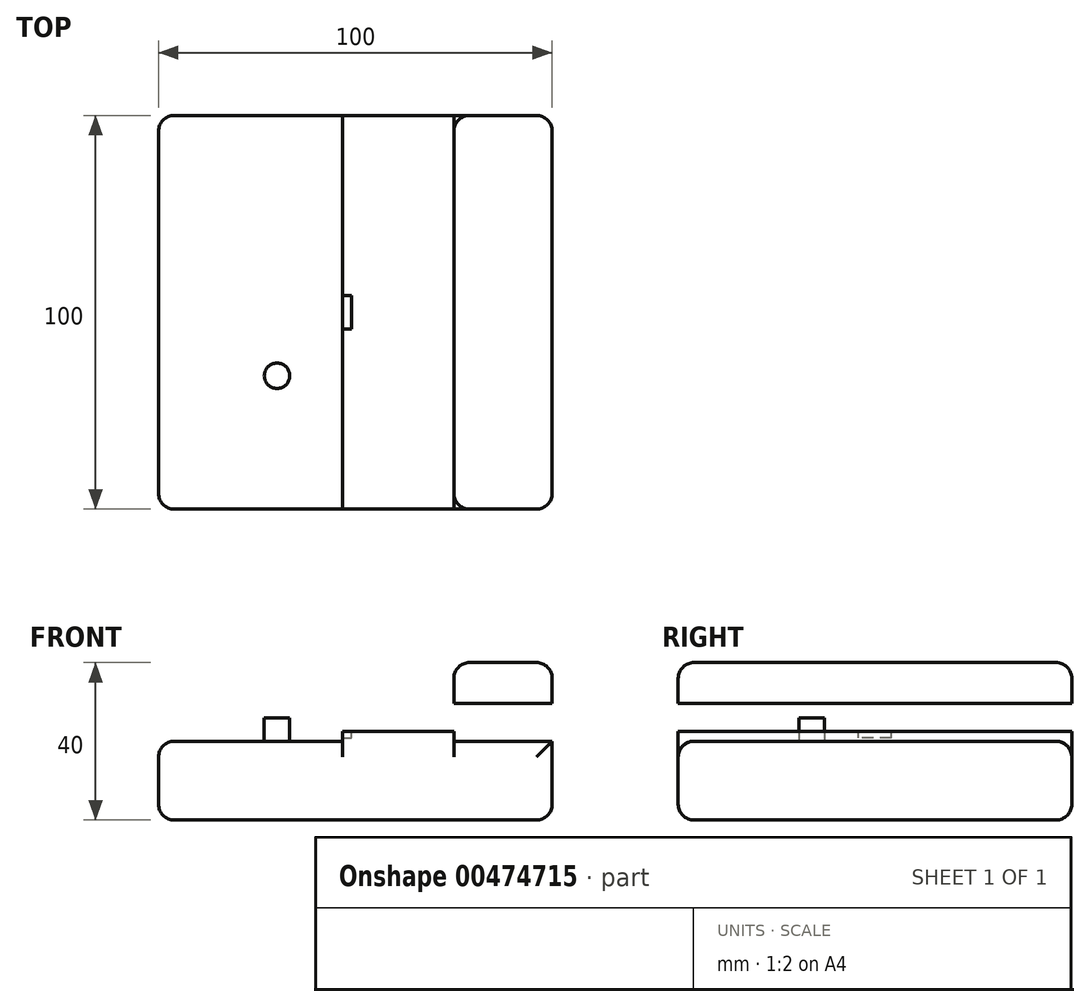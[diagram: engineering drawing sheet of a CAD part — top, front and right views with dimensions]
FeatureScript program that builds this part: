
annotation { "Feature Type Name" : "Feature", "Feature Type Description" : "" }
export const myFeature = defineFeature(function(context is Context, id is Id, definition is map)
    precondition{}
    {
        {
            var Q0;
            Q0=qCreatedBy(makeId("Top.planeOp"),FACE);
            var sketch = newSketch(context, id + "F0", { "sketchPlane" : qUnion([Q0])});
            skLineSegment(sketch, "E0.bottom", {"start": v(50, -50) * mm, "end": v(-50, -50) * mm});
            skLineSegment(sketch, "E0.top", {"start": v(50, 50) * mm, "end": v(-50, 50) * mm});
            skLineSegment(sketch, "E0.left", {"start": v(50, -50) * mm, "end": v(50, 50) * mm});
            skLineSegment(sketch, "E0.right", {"start": v(-50, -50) * mm, "end": v(-50, 50) * mm});
            skPoint(sketch, "E0.middle", {"position": v(0, 0) * mm});
            skSolve(sketch);
        }
        {
            var Q0;
            Q0=makeQuery(id+"F0.imprint","IMPRINT",FACE,{"disambiguationData":[TD([[makeQuery(id+"F0.imprint","IMPRINT",EDGE,{"derivedFrom":sQuery(id+"F0.wireOp",EDGE,"E0.bottom")}),-1.0]])]});
            extrude(context, id + "F1", {"entities" : qUnion([Q0]), "endBound" : BoundingType.SYMMETRIC, "depth" : 20 * mm, "offsetDistance" : 25 * mm});
        }
        {
            var Q0;
            Q0=makeQuery(id+"F1.opExtrude","CAP_FACE",FACE,{"disambiguationData":[OSD([sQuery(id+"F0.wireOp",EDGE,"E0.bottom"),sQuery(id+"F0.wireOp",EDGE,"E0.top"),sQuery(id+"F0.wireOp",EDGE,"E0.left"),sQuery(id+"F0.wireOp",EDGE,"E0.right")])],"isStart":false});
            var sketch = newSketch(context, id + "F2", { "sketchPlane" : qUnion([Q0])});
            skLineSegment(sketch, "E1.0.0", {"start": v(50, -50) * mm, "end": v(50, 50) * mm});
            skLineSegment(sketch, "E1.0.1", {"start": v(50, 50) * mm, "end": v(-50, 50) * mm});
            skLineSegment(sketch, "E1.0.2", {"start": v(-50, 50) * mm, "end": v(-50, -50) * mm});
            skLineSegment(sketch, "E1.0.3", {"start": v(-50, -50) * mm, "end": v(50, -50) * mm});
            skLineSegment(sketch, "E2", {"start": v(25, 0) * mm, "end": v(25, -50) * mm});
            skLineSegment(sketch, "E3", {"start": v(25, -50) * mm, "end": v(25, 50) * mm});
            skPoint(sketch, "E4.start.orphan", {"position": v(50, 0) * mm});
            skSolve(sketch);
        }
        {
            var Q0;
            Q0=makeQuery(id+"F1.opExtrude","SWEPT_FACE",FACE,{"disambiguationData":[OSD([sQuery(id+"F0.wireOp",EDGE,"E0.bottom")])]});
            var sketch = newSketch(context, id + "F3", { "sketchPlane" : qUnion([Q0])});
            skLineSegment(sketch, "E5.0.0", {"start": v(-50, -10) * mm, "end": v(50, -10) * mm});
            skLineSegment(sketch, "E5.0.1", {"start": v(50, -10) * mm, "end": v(50, 10) * mm});
            skLineSegment(sketch, "E5.0.2", {"start": v(50, 10) * mm, "end": v(-50, 10) * mm});
            skLineSegment(sketch, "E5.0.3", {"start": v(-50, 10) * mm, "end": v(-50, -10) * mm});
            skLineSegment(sketch, "E6", {"start": v(50, 10) * mm, "end": v(25, 10) * mm});
            skLineSegment(sketch, "E7", {"start": v(25, 10) * mm, "end": v(0, 10) * mm});
            skLineSegment(sketch, "E8", {"start": v(0, 10) * mm, "end": v(0, 22.2) * mm});
            skLineSegment(sketch, "E9", {"start": v(0, 16.1) * mm, "end": v(25, 16.1) * mm});
            skLineSegment(sketch, "E10", {"start": v(25, 16.1) * mm, "end": v(25, 12.56) * mm});
            skLineSegment(sketch, "E11", {"start": v(25, 12.56) * mm, "end": v(25, 19.64) * mm});
            skLineSegment(sketch, "E12", {"start": v(25, 10) * mm, "end": v(25, 12.56) * mm});
            skLineSegment(sketch, "E13", {"start": v(50, 10) * mm, "end": v(50, 19.64) * mm});
            skLineSegment(sketch, "E14", {"start": v(25, 19.64) * mm, "end": v(50, 19.64) * mm});
            skLineSegment(sketch, "E15", {"start": v(50, 10) * mm, "end": v(50, 30) * mm});
            skLineSegment(sketch, "E16", {"start": v(50, 30) * mm, "end": v(25, 30) * mm});
            skLineSegment(sketch, "E17", {"start": v(25, 30) * mm, "end": v(25, 19.64) * mm});
            skSolve(sketch);
        }
        {
            var Q0;
            {var subQ4=sQuery(id+"F3.wireOp",EDGE,"E6");Q0=makeQuery(id+"F3.imprint","IMPRINT",FACE,{"disambiguationData":[TD([[makeQuery(id+"F3.imprint","IMPRINT",EDGE,{"derivedFrom":subQ4}),-1.0]])]});}
            var Q1;
            {var subQ0=sQuery(id+"F3.wireOp",EDGE,"E14");Q1=makeQuery(id+"F3.imprint","IMPRINT",FACE,{"disambiguationData":[TD([[makeQuery(id+"F3.imprint","IMPRINT",EDGE,{"derivedFrom":subQ0}),1.0]])]});}
            extrude(context, id + "F4", {"entities" : qUnion([Q0, Q1]), "operationType" : NewBodyOperationType.ADD, "oppositeDirection" : true, "depth" : 100 * mm, "offsetDistance" : 25 * mm});
        }
        {
            var Q0;
            Q0=makeQuery(id+"F4.opExtrude","SWEPT_FACE",FACE,{"disambiguationData":[OSD([sQuery(id+"F3.wireOp",EDGE,"E11"),sQuery(id+"F3.wireOp",EDGE,"E12"),sQuery(id+"F3.wireOp",EDGE,"E17")])]});
            var sketch = newSketch(context, id + "F5", { "sketchPlane" : qUnion([Q0])});
            skLineSegment(sketch, "E18.0.0", {"start": v(50, 10) * mm, "end": v(50, 30) * mm});
            skLineSegment(sketch, "E18.0.1", {"start": v(50, 30) * mm, "end": v(-50, 30) * mm});
            skLineSegment(sketch, "E18.0.2", {"start": v(-50, 30) * mm, "end": v(-50, 10) * mm});
            skLineSegment(sketch, "E18.0.3", {"start": v(-50, 10) * mm, "end": v(50, 10) * mm});
            skLineSegment(sketch, "E19", {"start": v(0, 12.55) * mm, "end": v(0, 13.4) * mm});
            skLineSegment(sketch, "E20", {"start": v(50, 11.71) * mm, "end": v(50, 10) * mm});
            skLineSegment(sketch, "E21", {"start": v(-50, 11.71) * mm, "end": v(-50, 10) * mm});
            skCircle(sketch, "E22", {"center": v(0, 16.94) * mm, "radius": 3.54 * mm});
            skLineSegment(sketch, "E23", {"start": v(0, 12.55) * mm, "end": v(-50, 12.55) * mm});
            skLineSegment(sketch, "E24", {"start": v(-50, 12.55) * mm, "end": v(-50, 10) * mm});
            skLineSegment(sketch, "E25", {"start": v(0, 12.55) * mm, "end": v(50, 12.55) * mm});
            skLineSegment(sketch, "E26", {"start": v(50, 12.55) * mm, "end": v(50, 10) * mm});
            skPoint(sketch, "E27.orphan", {"position": v(0, 10) * mm});
            skLineSegment(sketch, "E28", {"start": v(0, 16.94) * mm, "end": v(0, 13.4) * mm});
            skLineSegment(sketch, "E29", {"start": v(0, 12.55) * mm, "end": v(0, 10) * mm});
            skSolve(sketch);
        }
        {
            var Q0;
            Q0=makeQuery(id+"F5.imprint","IMPRINT",FACE,{"disambiguationData":[TD([[makeQuery(id+"F5.imprint","IMPRINT",EDGE,{"derivedFrom":sQuery(id+"F5.wireOp",EDGE,"E22")}),1.0]])]});
            extrude(context, id + "F6", {"entities" : qUnion([Q0]), "operationType" : NewBodyOperationType.REMOVE, "oppositeDirection" : true, "depth" : 4.04 * mm, "offsetDistance" : 25 * mm});
        }
        {
            var Q0;
            {var subQ4=sQuery(id+"F5.wireOp",EDGE,"E25");Q0=makeQuery(id+"F5.imprint","IMPRINT",FACE,{"disambiguationData":[TD([[makeQuery(id+"F5.imprint","IMPRINT",EDGE,{"derivedFrom":subQ4}),-1.0]])]});}
            var Q1;
            {var subQ4=sQuery(id+"F5.wireOp",EDGE,"E23");Q1=makeQuery(id+"F5.imprint","IMPRINT",FACE,{"disambiguationData":[TD([[makeQuery(id+"F5.imprint","IMPRINT",EDGE,{"derivedFrom":subQ4}),1.0]])]});}
            extrude(context, id + "F7", {"entities" : qUnion([Q0, Q1]), "operationType" : NewBodyOperationType.ADD, "depth" : 28.23 * mm, "offsetDistance" : 25 * mm});
        }
        {
            var Q0;
            Q0=makeQuery(id+"F7.opExtrude","CAP_FACE",FACE,{"disambiguationData":[OSD([sQuery(id+"F5.wireOp",EDGE,"E18.0.3"),sQuery(id+"F5.wireOp",EDGE,"9pRNRzZh-An68-irgO-cDjF-4OQsVo2mt1ul"),sQuery(id+"F5.wireOp",EDGE,"E20"),sQuery(id+"F5.wireOp",EDGE,"OAPvk0ag-MwiS-kipx-ZiEZ-sf6YjjynKVG3"),sQuery(id+"F5.wireOp",EDGE,"E21")])],"isStart":false});
            var sketch = newSketch(context, id + "F8", { "sketchPlane" : qUnion([Q0])});
            skLineSegment(sketch, "E30.0", {"start": v(0, 12.55) * mm, "end": v(0, 13.4) * mm});
            skPoint(sketch, "E31.center.orphan", {"position": v(0, 12.97) * mm});
            skLineSegment(sketch, "E32", {"start": v(0, 10) * mm, "end": v(0, 13.4) * mm});
            skCircle(sketch, "E33", {"center": v(0, 16.94) * mm, "radius": 6.1 * mm});
            skLineSegment(sketch, "E34", {"start": v(0, 10.84) * mm, "end": v(0, 12.55) * mm});
            skLineSegment(sketch, "E35", {"start": v(0, 10) * mm, "end": v(0, 10.84) * mm});
            skCircle(sketch, "E36", {"center": v(0, 16.94) * mm, "radius": 3.96 * mm});
            skCircle(sketch, "E37", {"center": v(0, 16.94) * mm, "radius": 3.54 * mm});
            skLineSegment(sketch, "E38", {"start": v(0, 10) * mm, "end": v(0, 24.14) * mm});
            skSolve(sketch);
        }
        {
            var Q0;
            {var subQ0=sQuery(id+"F8.wireOp",EDGE,"E38");var subQ1=sQuery(id+"F8.wireOp",EDGE,"E33");var subQ2=makeQuery(id+"F8.imprint","INTERSECT",VERTEX,{"disambiguationData":[OD(1.0)],"derivedFrom":[subQ1,subQ0]});Q0=makeQuery(id+"F8.imprint","IMPRINT",FACE,{"disambiguationData":[TD([[makeQuery(id+"F8.imprint","IMPRINT",EDGE,{"disambiguationData":[TD([[subQ2,1.0]])],"derivedFrom":subQ1}),1.0]])]});}
            var Q1;
            {var subQ0=sQuery(id+"F8.wireOp",EDGE,"E38");var subQ1=sQuery(id+"F8.wireOp",EDGE,"E33");var subQ2=makeQuery(id+"F8.imprint","INTERSECT",VERTEX,{"disambiguationData":[OD(1.0)],"derivedFrom":[subQ1,subQ0]});Q1=makeQuery(id+"F8.imprint","IMPRINT",FACE,{"disambiguationData":[TD([[makeQuery(id+"F8.imprint","IMPRINT",EDGE,{"disambiguationData":[TD([[subQ2,-1.0]])],"derivedFrom":subQ1}),1.0]])]});}
            extrude(context, id + "F9", {"entities" : qUnion([Q0, Q1]), "operationType" : NewBodyOperationType.REMOVE, "oppositeDirection" : true, "depth" : 2.25 * mm, "offsetDistance" : 25 * mm});
        }
        {
            var Q0;
            {var subQ4=sQuery(id+"F2.wireOp",EDGE,"E1.0.2");Q0=makeQuery(id+"F2.imprint","IMPRINT",FACE,{"disambiguationData":[TD([[makeQuery(id+"F2.imprint","IMPRINT",EDGE,{"derivedFrom":subQ4}),-1.0]])]});}
            var sketch = newSketch(context, id + "F10", { "sketchPlane" : qUnion([Q0])});
            skLineSegment(sketch, "E39.0.0", {"start": v(-3.24, 4.24) * mm, "end": v(-3.24, -4.24) * mm});
            skLineSegment(sketch, "E39.0.1", {"start": v(-3.24, -4.24) * mm, "end": v(-0.99, -4.24) * mm});
            skLineSegment(sketch, "E39.0.2", {"start": v(-0.99, -4.24) * mm, "end": v(-0.99, 4.24) * mm});
            skLineSegment(sketch, "E39.0.3", {"start": v(-0.99, 4.24) * mm, "end": v(-3.24, 4.24) * mm});
            skLineSegment(sketch, "E40.0.0", {"start": v(-50, -50) * mm, "end": v(25, -50) * mm});
            skLineSegment(sketch, "E40.0.1", {"start": v(25, -50) * mm, "end": v(25, 0) * mm});
            skLineSegment(sketch, "E40.0.2", {"start": v(25, 0) * mm, "end": v(25, 50) * mm});
            skLineSegment(sketch, "E40.0.3", {"start": v(25, 50) * mm, "end": v(-50, 50) * mm});
            skLineSegment(sketch, "E40.0.4", {"start": v(-50, 50) * mm, "end": v(-50, -50) * mm});
            skLineSegment(sketch, "E41", {"start": v(-0.99, 0) * mm, "end": v(-19.9, 0) * mm});
            skLineSegment(sketch, "E42", {"start": v(-19.9, 0) * mm, "end": v(-19.9, -16.13) * mm});
            skCircle(sketch, "E43", {"center": v(-19.9, -16.13) * mm, "radius": 3.24 * mm});
            skSolve(sketch);
        }
        {
            var Q0;
            Q0=makeQuery(id+"F10.imprint","IMPRINT",FACE,{"disambiguationData":[TD([[makeQuery(id+"F10.imprint","IMPRINT",EDGE,{"derivedFrom":sQuery(id+"F10.wireOp",EDGE,"E43")}),1.0]])]});
            extrude(context, id + "F11", {"entities" : qUnion([Q0]), "operationType" : NewBodyOperationType.ADD, "depth" : 5.97 * mm, "offsetDistance" : 25 * mm});
        }
        {
            var Q0;
            Q0=makeQuery(id+"F4.opExtrude","SWEPT_EDGE",EDGE,{"disambiguationData":[OSD([sQuery(id+"F3.wireOp",EDGE,"E16"),sQuery(id+"F3.wireOp",EDGE,"E17")])]});
            var Q1;
            Q1=makeQuery(id+"F4.opExtrude","SWEPT_EDGE",EDGE,{"disambiguationData":[OSD([sQuery(id+"F3.wireOp",EDGE,"E15"),sQuery(id+"F3.wireOp",EDGE,"E16")])]});
            var Q2;
            Q2=makeQuery(id+"F1.opExtrude","CAP_EDGE",EDGE,{"disambiguationData":[OSD([sQuery(id+"F0.wireOp",EDGE,"E0.right")])],"isStart":false});
            var Q3;
            Q3=makeQuery(id+"F1.opExtrude","CAP_EDGE",EDGE,{"disambiguationData":[OSD([sQuery(id+"F0.wireOp",EDGE,"E0.right")])],"isStart":true});
            var Q4;
            Q4=makeQuery(id+"F1.opExtrude","CAP_EDGE",EDGE,{"disambiguationData":[OSD([sQuery(id+"F0.wireOp",EDGE,"E0.left")])],"isStart":true});
            var Q5;
            Q5=makeQuery(id+"F4.opExtrude","CAP_EDGE",EDGE,{"disambiguationData":[OSD([sQuery(id+"F3.wireOp",EDGE,"E11"),sQuery(id+"F3.wireOp",EDGE,"E12"),sQuery(id+"F3.wireOp",EDGE,"E17")])],"isStart":true});
            var Q6;
            Q6=makeQuery(id+"F4.opExtrude","CAP_EDGE",EDGE,{"disambiguationData":[OSD([sQuery(id+"F3.wireOp",EDGE,"E16")])],"isStart":true});
            var Q7;
            Q7=makeQuery(id+"F4.boolean.opBoolean","MERGE",EDGE,{"derivedFrom":[makeQuery(id+"F1.opExtrude","SWEPT_EDGE",EDGE,{"disambiguationData":[OSD([sQuery(id+"F0.wireOp",EDGE,"E0.bottom"),sQuery(id+"F0.wireOp",EDGE,"E0.left")])]}),makeQuery(id+"F4.opExtrude","CAP_EDGE",EDGE,{"disambiguationData":[OSD([sQuery(id+"F3.wireOp",EDGE,"E15")])],"isStart":true})]});
            var Q8;
            Q8=makeQuery(id+"F1.opExtrude","CAP_EDGE",EDGE,{"disambiguationData":[OSD([sQuery(id+"F0.wireOp",EDGE,"E0.bottom")])],"isStart":true});
            var Q9;
            Q9=makeQuery(id+"F1.opExtrude","SWEPT_EDGE",EDGE,{"disambiguationData":[OSD([sQuery(id+"F0.wireOp",EDGE,"E0.bottom"),sQuery(id+"F0.wireOp",EDGE,"E0.right")])]});
            var Q10;
            Q10=makeQuery(id+"F1.opExtrude","SWEPT_EDGE",EDGE,{"disambiguationData":[OSD([sQuery(id+"F0.wireOp",EDGE,"E0.top"),sQuery(id+"F0.wireOp",EDGE,"E0.right")])]});
            var Q11;
            Q11=makeQuery(id+"F1.opExtrude","CAP_EDGE",EDGE,{"disambiguationData":[OSD([sQuery(id+"F0.wireOp",EDGE,"E0.top")])],"isStart":false});
            var Q12;
            Q12=makeQuery(id+"F4.opExtrude","CAP_EDGE",EDGE,{"disambiguationData":[OSD([sQuery(id+"F3.wireOp",EDGE,"E11"),sQuery(id+"F3.wireOp",EDGE,"E12"),sQuery(id+"F3.wireOp",EDGE,"E17")])],"isStart":false});
            var Q13;
            Q13=makeQuery(id+"F4.opExtrude","CAP_EDGE",EDGE,{"disambiguationData":[OSD([sQuery(id+"F3.wireOp",EDGE,"E16")])],"isStart":false});
            var Q14;
            Q14=makeQuery(id+"F4.boolean.opBoolean","MERGE",EDGE,{"derivedFrom":[makeQuery(id+"F1.opExtrude","SWEPT_EDGE",EDGE,{"disambiguationData":[OSD([sQuery(id+"F0.wireOp",EDGE,"E0.top"),sQuery(id+"F0.wireOp",EDGE,"E0.left")])]}),makeQuery(id+"F4.opExtrude","CAP_EDGE",EDGE,{"disambiguationData":[OSD([sQuery(id+"F3.wireOp",EDGE,"E15")])],"isStart":false})]});
            var Q15;
            Q15=makeQuery(id+"F1.opExtrude","CAP_EDGE",EDGE,{"disambiguationData":[OSD([sQuery(id+"F0.wireOp",EDGE,"E0.top")])],"isStart":true});
            var Q16;
            Q16=makeQuery(id+"F1.opExtrude","CAP_EDGE",EDGE,{"disambiguationData":[OSD([sQuery(id+"F0.wireOp",EDGE,"E0.bottom")])],"isStart":false});
            fillet(context, id + "F12", {"entities" : qUnion([Q0, Q1, Q2, Q3, Q4, Q5, Q6, Q7, Q8, Q9, Q10, Q11, Q12, Q13, Q14, Q15, Q16]), "radius" : 4 * mm, "tangentPropagation" : true, "allowEdgeOverflow" : false});
        }
        {
            var Q0;
            Q0=makeQuery(id+"F7.opExtrude","SWEPT_FACE",FACE,{"disambiguationData":[OSD([sQuery(id+"F5.wireOp",EDGE,"E23"),sQuery(id+"F5.wireOp",EDGE,"E25")])]});
            var sketch = newSketch(context, id + "F13", { "sketchPlane" : qUnion([Q0])});
            skLineSegment(sketch, "E44.0.0", {"start": v(-3.24, 4.24) * mm, "end": v(-3.24, -4.24) * mm});
            skLineSegment(sketch, "E44.0.1", {"start": v(-3.24, -4.24) * mm, "end": v(-0.99, -4.24) * mm});
            skLineSegment(sketch, "E44.0.2", {"start": v(-0.99, -4.24) * mm, "end": v(-0.99, 4.24) * mm});
            skLineSegment(sketch, "E44.0.3", {"start": v(-0.99, 4.24) * mm, "end": v(-3.24, 4.24) * mm});
            skSolve(sketch);
        }
        {
            var Q0;
            Q0 = qSketchRegion(id + "F13", true);
            extrude(context, id + "F14", {"entities" : qUnion([Q0]), "operationType" : NewBodyOperationType.REMOVE, "oppositeDirection" : true, "depth" : 1.73 * mm, "offsetDistance" : 25 * mm});
        }
    });
